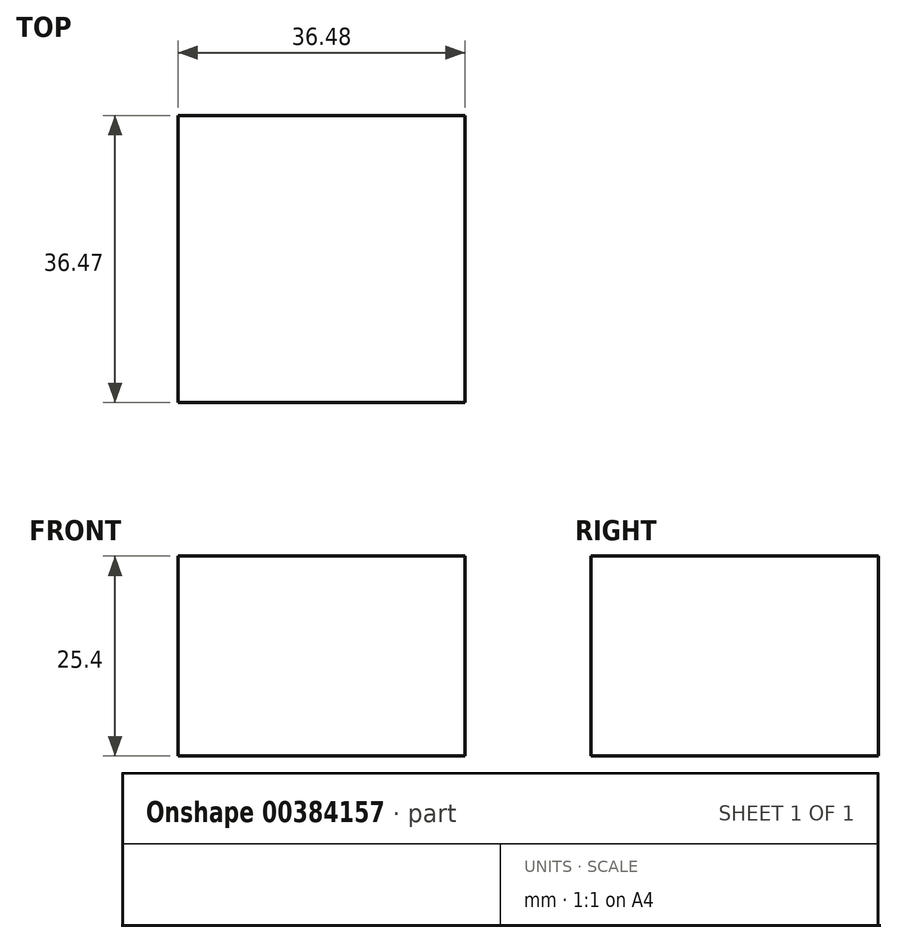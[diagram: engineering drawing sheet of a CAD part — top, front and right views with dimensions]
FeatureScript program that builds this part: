
annotation { "Feature Type Name" : "Feature", "Feature Type Description" : "" }
export const myFeature = defineFeature(function(context is Context, id is Id, definition is map)
    precondition{}
    {
        {
            var Q0;
            Q0=qCreatedBy(makeId("Top.planeOp"),FACE);
            var sketch = newSketch(context, id + "F0", { "sketchPlane" : qUnion([Q0])});
            skLineSegment(sketch, "E0", {"start": v(0, 0) * mm, "end": v(0, 36.47) * mm});
            skLineSegment(sketch, "E1", {"start": v(0, 36.47) * mm, "end": v(36.48, 36.47) * mm});
            skLineSegment(sketch, "E2", {"start": v(36.48, 36.47) * mm, "end": v(36.48, 0) * mm});
            skLineSegment(sketch, "E3", {"start": v(36.48, 0) * mm, "end": v(0, 0) * mm});
            skSolve(sketch);
        }
        {
            var Q0;
            Q0 = qSketchRegion(id + "F0", true);
            extrude(context, id + "F1", {"entities" : qUnion([Q0]), "depth" : 25.4 * mm});
        }
    });
